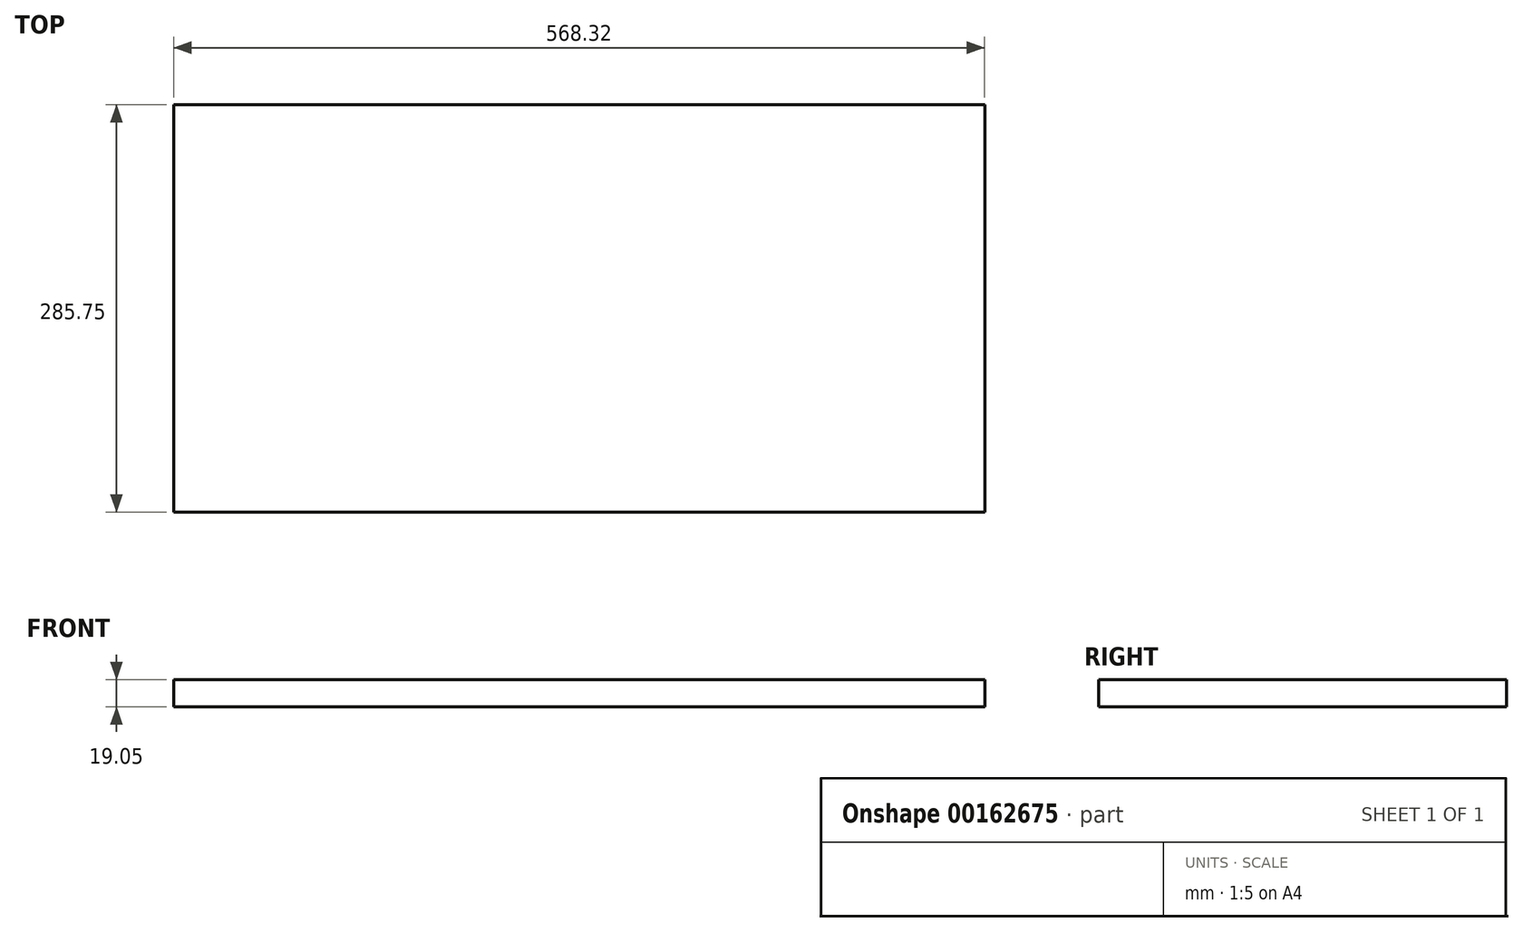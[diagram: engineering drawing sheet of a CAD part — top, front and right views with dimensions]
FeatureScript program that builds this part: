
annotation { "Feature Type Name" : "Feature", "Feature Type Description" : "" }
export const myFeature = defineFeature(function(context is Context, id is Id, definition is map)
    precondition{}
    {
        {
            var Q0;
            Q0=qCreatedBy(makeId("Top.planeOp"),FACE);
            var sketch = newSketch(context, id + "F0", { "sketchPlane" : qUnion([Q0])});
            skLineSegment(sketch, "E0.bottom", {"start": v(-125.21, 207.72) * mm, "end": v(443.11, 207.72) * mm});
            skLineSegment(sketch, "E0.top", {"start": v(-125.21, -78.03) * mm, "end": v(443.11, -78.03) * mm});
            skLineSegment(sketch, "E0.left", {"start": v(-125.21, 207.72) * mm, "end": v(-125.21, -78.03) * mm});
            skLineSegment(sketch, "E0.right", {"start": v(443.11, 207.72) * mm, "end": v(443.11, -78.03) * mm});
            skSolve(sketch);
        }
        {
            var Q0;
            Q0=makeQuery(id+"F0.imprint","IMPRINT",FACE,{"disambiguationData":[TD([[makeQuery(id+"F0.imprint","IMPRINT",EDGE,{"derivedFrom":sQuery(id+"F0.wireOp",EDGE,"E0.bottom")}),-1.0]])]});
            extrude(context, id + "F1", {"entities" : qUnion([Q0]), "depth" : 19.05 * mm});
        }
    });
